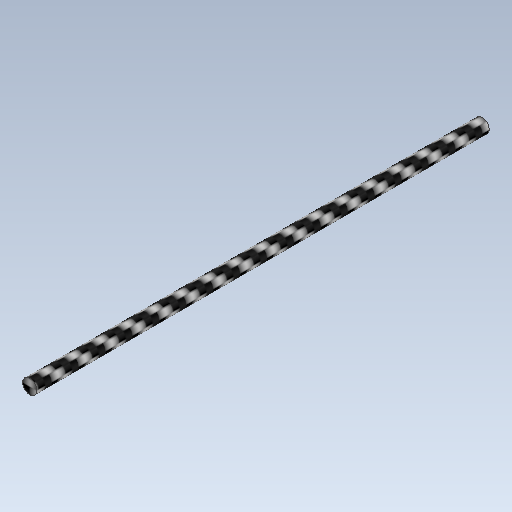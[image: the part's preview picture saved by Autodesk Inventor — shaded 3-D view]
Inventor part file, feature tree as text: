
AUTODESK INVENTOR PART (.ipt)
format: ipt  version: 2020 (Build 240168000, 168)  size: 107,520 bytes
history: native  units: in
note: dims shown in document units (in); Inventor stores cm internally (conversion verified against a paired STEP export)
features: extrude x1, sketch x1
ambient origin geometry x8: Origin, YZ Plane, XZ Plane, XY Plane, X Axis, Y Axis, Z Axis, Center Point
bodies: Solid1 (feature_tree)
feature tree (2):
  extrude  "Extrusion1"  Depth=2.4807in
  sketch  "Sketch1"  dims[d0=0.0787in d1=2.4807in d2=0.0in]
